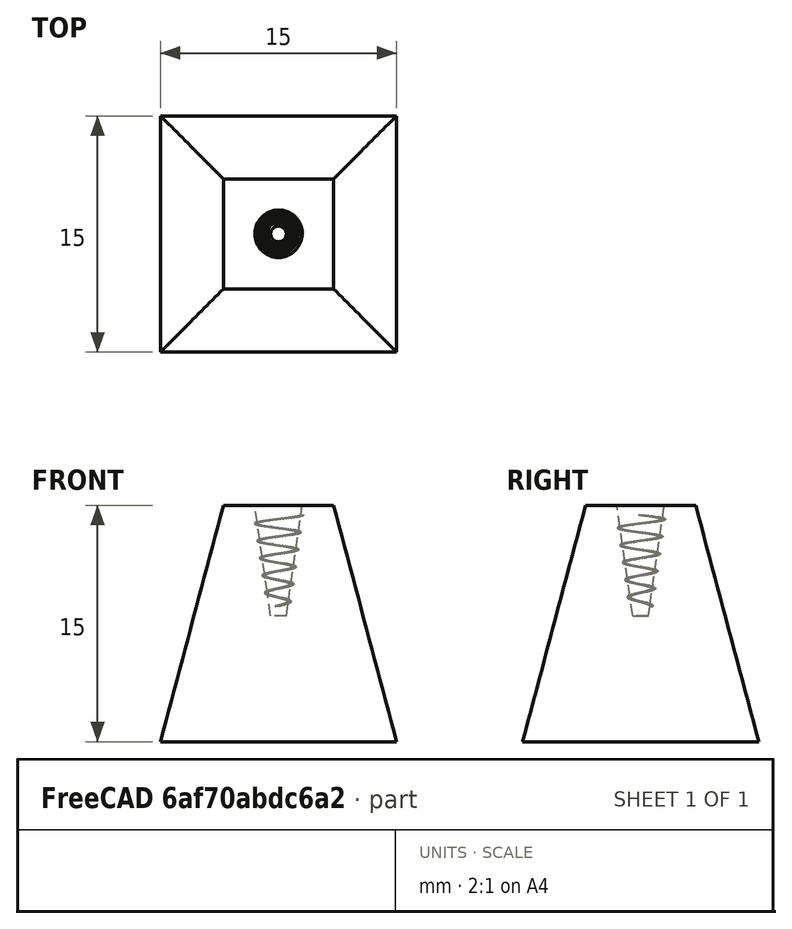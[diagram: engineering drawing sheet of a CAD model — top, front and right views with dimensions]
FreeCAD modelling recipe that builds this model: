
FCSTD DOCUMENT  (FreeCAD 1.2R20251230 (Git shallow))
Label: tapered_square_standoff_15x15_to_7x7
License: Creative Commons Attribution 4.0
LicenseURL: https://creativecommons.org/licenses/by/4.0/
objects: Part::Feature×3, Sketcher::SketchObject×2, Part::Cut×2, App::Point×1, PartDesign::Body×1
note: 10 computed .brp shape members not serialized (recipe doc carries the construction recipe); baked Part::Feature solids carry a one-line shape summary decoded from their .brp

FEATURE [App::Point] Origin001
  Role = Origin
FEATURE [Sketcher::SketchObject] Sketch_01_BaseSquare_15x15
  ArcFitTolerance = 1e-06
  ExternalTypes = [0]
  FullyConstrained = false
  MakeInternals = false
  sketch-geometry (4):
    g0: LineSegment StartX=-7.5 StartY=-7.5 StartZ=0 EndX=7.5 EndY=-7.5 EndZ=0
    g1: LineSegment StartX=7.5 StartY=-7.5 StartZ=0 EndX=7.5 EndY=7.5 EndZ=0
    g2: LineSegment StartX=7.5 StartY=7.5 StartZ=0 EndX=-7.5 EndY=7.5 EndZ=0
    g3: LineSegment StartX=-7.5 StartY=7.5 StartZ=0 EndX=-7.5 EndY=-7.5 EndZ=0
  constraints (4):
    c: Coincident(g0,g1)
    c: Coincident(g1,g2)
    c: Coincident(g2,g3)
    c: Coincident(g3,g0)
FEATURE [Sketcher::SketchObject] Sketch_02_TopSquare_7x7
  ArcFitTolerance = 1e-06
  ExternalTypes = [0]
  FullyConstrained = false
  MakeInternals = false
  Placement = pos=(0,0,15) rot=(0,0,1;0rad)
  sketch-geometry (4):
    g0: LineSegment StartX=-3.5 StartY=-3.5 StartZ=0 EndX=3.5 EndY=-3.5 EndZ=0
    g1: LineSegment StartX=3.5 StartY=-3.5 StartZ=0 EndX=3.5 EndY=3.5 EndZ=0
    g2: LineSegment StartX=3.5 StartY=3.5 StartZ=0 EndX=-3.5 EndY=3.5 EndZ=0
    g3: LineSegment StartX=-3.5 StartY=3.5 StartZ=0 EndX=-3.5 EndY=-3.5 EndZ=0
  constraints (4):
    c: Coincident(g0,g1)
    c: Coincident(g1,g2)
    c: Coincident(g2,g3)
    c: Coincident(g3,g0)
FEATURE [PartDesign::Body] Body_TaperedSquareStandoff
  AllowCompound = true
  Group = -> [Sketch_01_BaseSquare_15x15,Sketch_02_TopSquare_7x7]
  Origin = -> Origin
FEATURE [Part::Feature] _03_Loft_15x15_To_7x7_Height15
  shape: bbox 15 x 15 x 15 mm, 6 faces (baked)
FEATURE [Part::Feature] _04_Tool_Tapered_Center_Hole_3to1_Depth7
  shape: bbox 3 x 3 x 7 mm, 3 faces (baked)
FEATURE [Part::Cut] _05_Cut_Tapered_Center_Hole
  Base = -> _03_Loft_15x15_To_7x7_Height15
  Refine = true
  Tool = -> _04_Tool_Tapered_Center_Hole_3to1_Depth7
FEATURE [Part::Feature] _06_Tool_Internal_Thread_Groove
  shape: bbox 3.127 x 3.048 x 5.8 mm, 255 faces (baked)
FEATURE [Part::Cut] _07_Cut_Internal_Thread_Groove  label="Final_TaperedSquareStandoff"
  Base = -> _05_Cut_Tapered_Center_Hole
  Refine = true
  Tool = -> _06_Tool_Internal_Thread_Groove
